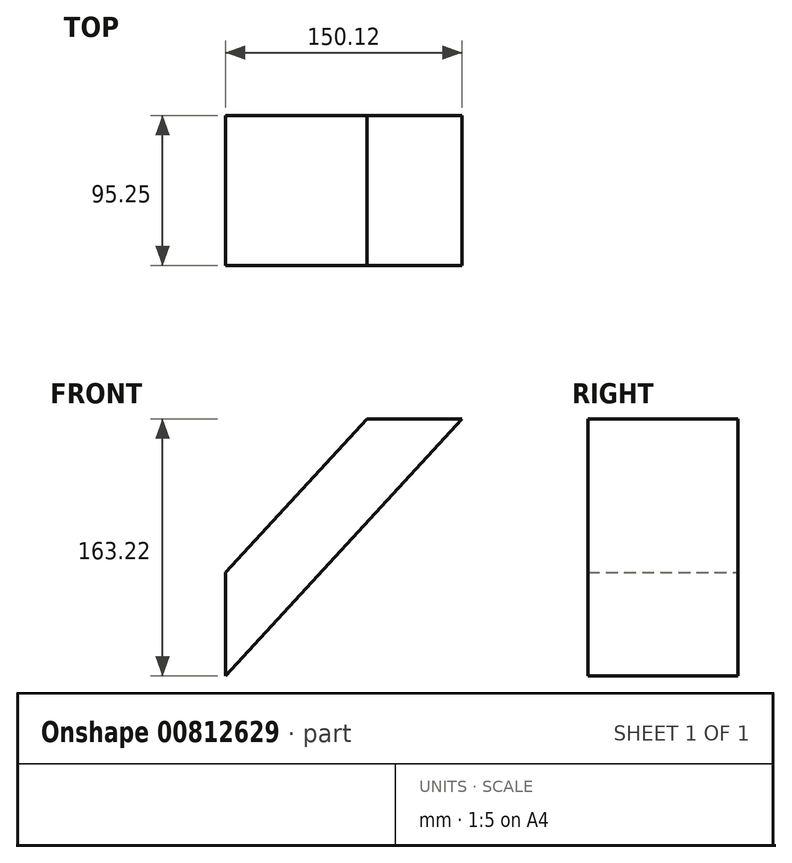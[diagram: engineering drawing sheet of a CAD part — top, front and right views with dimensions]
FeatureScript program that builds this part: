
annotation { "Feature Type Name" : "Feature", "Feature Type Description" : "" }
export const myFeature = defineFeature(function(context is Context, id is Id, definition is map)
    precondition{}
    {
        {
            var Q0;
            Q0=qCreatedBy(makeId("Front.planeOp"),FACE);
            var sketch = newSketch(context, id + "F0", { "sketchPlane" : qUnion([Q0])});
            skLineSegment(sketch, "E0", {"start": v(0, -97.56) * mm, "end": v(89.73, 0) * mm});
            skLineSegment(sketch, "E1", {"start": v(89.73, 0) * mm, "end": v(150.12, 0) * mm});
            skLineSegment(sketch, "E2", {"start": v(150.12, 0) * mm, "end": v(0, -163.22) * mm});
            skLineSegment(sketch, "E3", {"start": v(0, -163.22) * mm, "end": v(0, -97.56) * mm});
            skSolve(sketch);
        }
        {
            var Q0;
            Q0 = qSketchRegion(id + "F0", true);
            extrude(context, id + "F1", {"entities" : qUnion([Q0]), "depth" : 95.25 * mm, "offsetDistance" : 25.4 * mm});
        }
    });
